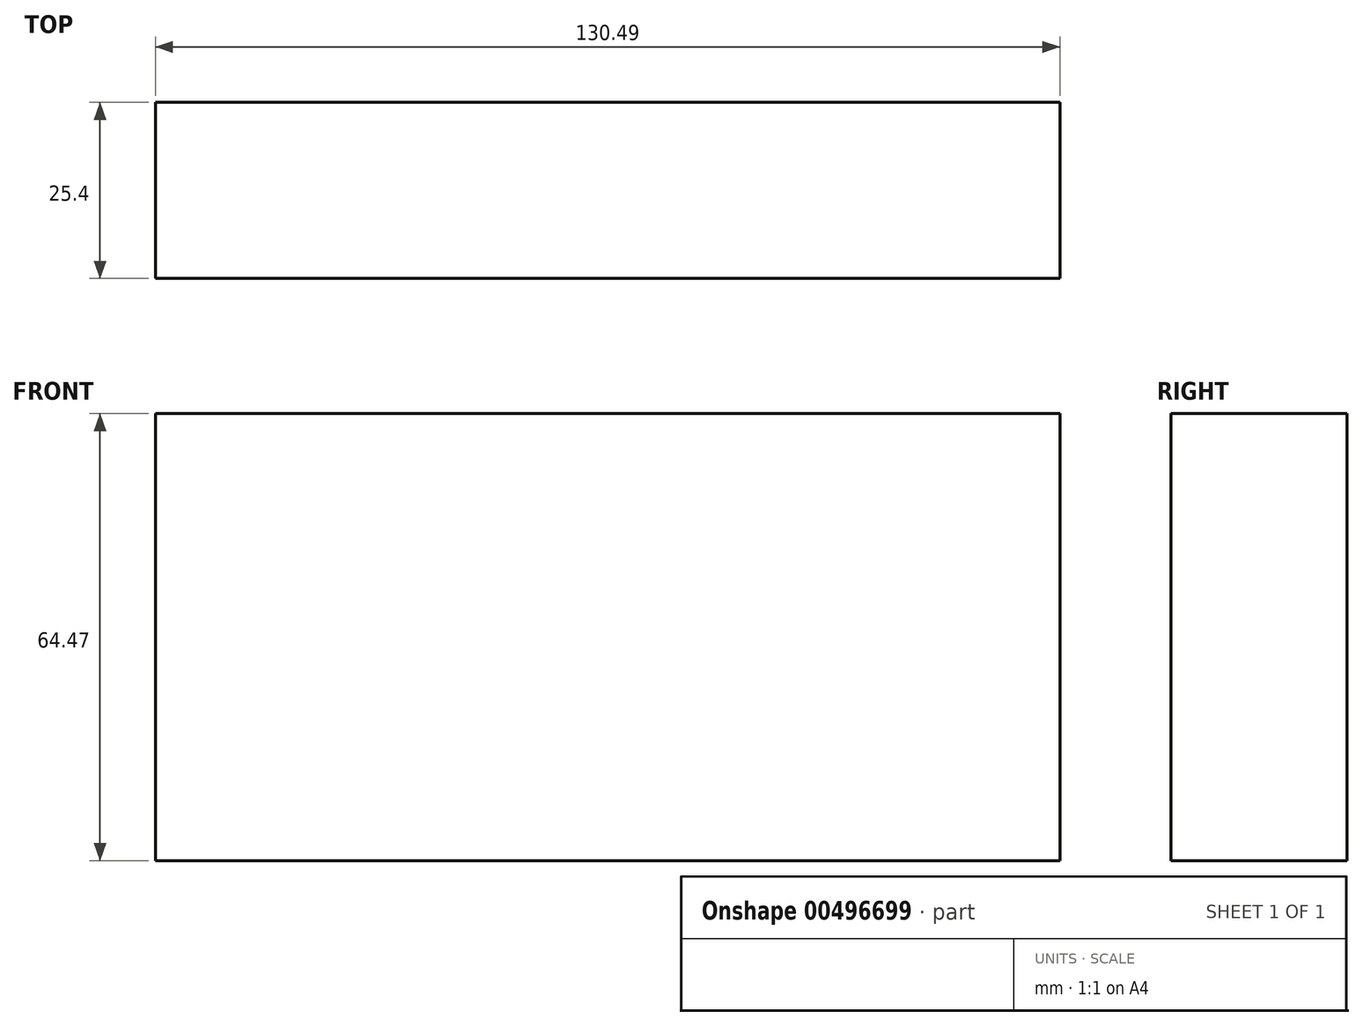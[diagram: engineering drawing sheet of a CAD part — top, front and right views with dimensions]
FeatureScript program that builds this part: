
annotation { "Feature Type Name" : "Feature", "Feature Type Description" : "" }
export const myFeature = defineFeature(function(context is Context, id is Id, definition is map)
    precondition{}
    {
        {
            var Q0;
            Q0=qCreatedBy(makeId("Front.planeOp"),FACE);
            var sketch = newSketch(context, id + "F0", { "sketchPlane" : qUnion([Q0])});
            skLineSegment(sketch, "E0.bottom", {"start": v(-60.97, 27.64) * mm, "end": v(69.52, 27.64) * mm});
            skLineSegment(sketch, "E0.top", {"start": v(-60.97, -36.83) * mm, "end": v(69.52, -36.83) * mm});
            skLineSegment(sketch, "E0.left", {"start": v(-60.97, 27.64) * mm, "end": v(-60.97, -36.83) * mm});
            skLineSegment(sketch, "E0.right", {"start": v(69.52, 27.64) * mm, "end": v(69.52, -36.83) * mm});
            skSolve(sketch);
        }
        {
            var Q0;
            Q0 = qSketchRegion(id + "F0", true);
            extrude(context, id + "F1", {"entities" : qUnion([Q0]), "depth" : 25.4 * mm});
        }
    });
